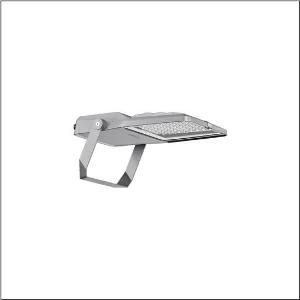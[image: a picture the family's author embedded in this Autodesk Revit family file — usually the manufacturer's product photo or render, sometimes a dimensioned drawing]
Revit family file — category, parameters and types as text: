
# Revit family: floodlight_fl_21_mini___pl43_5xa7773c2a1a_a3ea
name_source: partatom
category: Lighting Fixtures
units: mm (PartAtom-declared; Revit-internal decimal feet)

## family parameters
Cut with Voids When Loaded = No
Host = Face
Light Source = No
Part Type = Normal
Room Calculation Point = No
Round Connector Dimension = Use Diameter
Shared = No

## types (1)
- --- (1 x LED, 20010 lm, 163.5 W, 3000K)
    Apparent Load = 163 VA
    CIE Flux Codes = 27 78 99 100 100
    Color Rendering = 70
    Color Temperature = 3000K
    Default Elevation = 1800 mm
    Description = Floodlight FL 21 mini, floodlight, primary light control with lens, of PMMA, primary optical cover: protective disc, of toughened safety glass, transparent, light distribution: PL43, light emission: direct distribution, installation type: surface-mounted, LED, High Power LED, rated luminous flux: 20.010lm, luminous efficacy: 122lm/W, light colour: 730, colour temperature: 3000K, control: Temp-Guard, with terminal, 6-pole, mains connection: 220..240V, AC, 50/60Hz, start of lifetime: 164W, luminaire housing, of diecast aluminium, powder-coated, Siteco® metallic grey (DB 702S), corrosivity category C5 mid according to DIN EN ISO 12944, sealing non-destructively replaceable, mounting bracket, of steel, galvanised, powder-coated, Siteco® metallic grey (DB 702S), ON/OFF, protection rating (complete): IP66, insulation class (complete): insulation class I (protective earthing), certification: CE, ENEC, VDE, protection symbol: D, impact resistance: IK08, permissible operating ambient temperature: -40..+40°C, permissible operating ambient temperature for outdoor applications: -40..+50°C, standard: DIN EN 12944, LABS conformity tested according to VDMA 24364:2018-05, packaging unit: 1 piece

Light Distribution: PL43
    Height = 70 mm
    Lamp = 1 x LED
    Lamp Light Flux = 20010 lm
    Lamp Power = 163.5 W
    Lamp count = 1
    Length = 485 mm
    Luminous efficacy = 122 lm/W
    Manufacturer = Siteco
    ModVariant = No
    Model = 5XA7773C2A1A
    Number of Poles = 1
    OnlyDefault = Yes
    Power Factor = 1
    Product Name = Floodlight FL 21 mini | PL43
    Product group = floodlight | pylon annexe
    ProductGroupID = 6200
    Protection Class = Protection class I
    Protection Degree = IP 66
    RLX_Detail_Level = 1
    RLX_Emergency_Light_Flux = 0 lm
    RLX_Emergency_Type = 0
    RLX_Emergency_Type_DB = No
    RlxData = <blob elided: 94109 chars, md5=2da533b6>
    Socket = socket
    Standby Power = 0 W
    System Light Flux = 20010 lm
    System Power = 163 W
    Type Comments = factory setting: luminous flux: 100 % | (ON | - | - | - | - | - | - | -) | 825 mA
    Type Image = l_1006845.jpg
    URL = http://relux.com
    VarID = @adj_094677
    Voltage = 0 V
    Weight = 0.00 kg
    Width = 337 mm

## geometry (parser evidence)
native form markers: Blend x4, Sweep x13
no freeform markers — native parametric forms only
